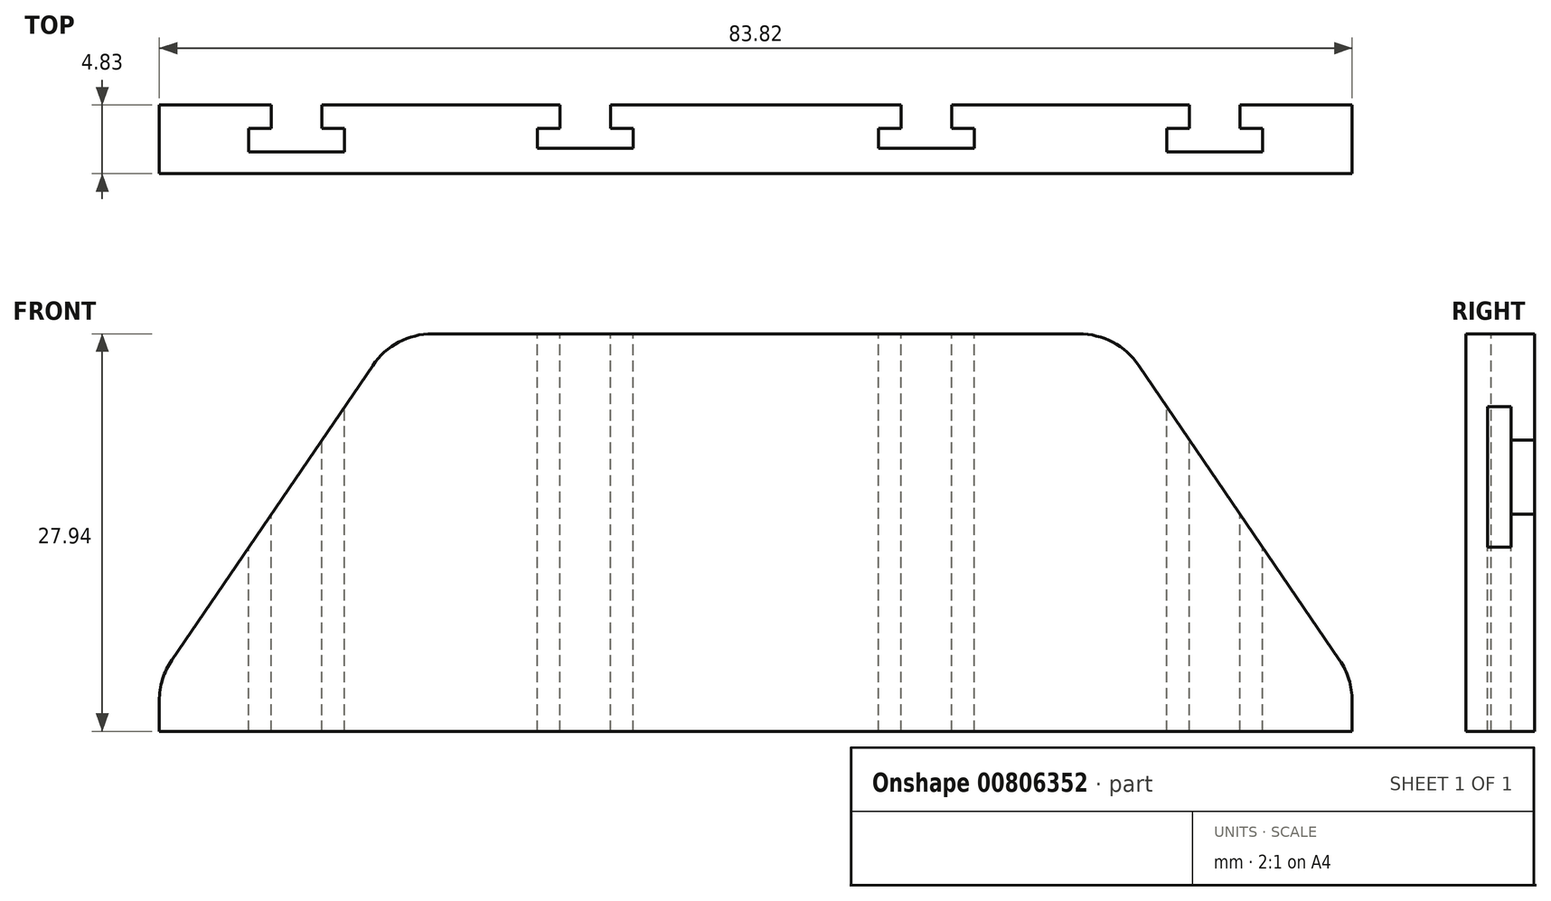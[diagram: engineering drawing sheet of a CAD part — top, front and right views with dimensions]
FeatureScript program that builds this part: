
annotation { "Feature Type Name" : "Feature", "Feature Type Description" : "" }
export const myFeature = defineFeature(function(context is Context, id is Id, definition is map)
    precondition{}
    {
        {
            var Q0;
            Q0=qCreatedBy(makeId("Front.planeOp"),FACE);
            var sketch = newSketch(context, id + "F0", { "sketchPlane" : qUnion([Q0])});
            skLineSegment(sketch, "E0", {"start": v(-44.45, -15.52) * mm, "end": v(-25.4, 12.42) * mm});
            skLineSegment(sketch, "E1", {"start": v(-25.4, 12.42) * mm, "end": v(25.4, 12.42) * mm});
            skLineSegment(sketch, "E2", {"start": v(25.4, 12.42) * mm, "end": v(44.45, -15.52) * mm});
            skLineSegment(sketch, "E3", {"start": v(44.45, -15.52) * mm, "end": v(-44.45, -15.52) * mm});
            skPoint(sketch, "E4", {"position": v(0, 12.42) * mm});
            skLineSegment(sketch, "E5.0", {"start": v(-23.39, 8.6) * mm, "end": v(23.39, 8.6) * mm});
            skLineSegment(sketch, "E5.1", {"start": v(-37.24, -11.71) * mm, "end": v(-23.39, 8.6) * mm});
            skLineSegment(sketch, "E5.2", {"start": v(37.24, -11.71) * mm, "end": v(-37.24, -11.71) * mm});
            skLineSegment(sketch, "E5.3", {"start": v(23.39, 8.6) * mm, "end": v(37.24, -11.71) * mm});
            skLineSegment(sketch, "E6", {"start": v(41.91, -1.58) * mm, "end": v(41.91, -22.95) * mm});
            skLineSegment(sketch, "E7.MirrorCS", {"start": v(-41.91, -1.58) * mm, "end": v(-41.91, -22.95) * mm});
            skSolve(sketch);
        }
        {
            var Q0;
            {var subQ1=sQuery(id+"F0.wireOp",EDGE,"E1");Q0=makeQuery(id+"F0.imprint","IMPRINT",FACE,{"disambiguationData":[TD([[makeQuery(id+"F0.imprint","IMPRINT",EDGE,{"derivedFrom":subQ1}),-1.0]])]});}
            var Q1;
            Q1=makeQuery(id+"F0.imprint","IMPRINT",FACE,{"disambiguationData":[TD([[makeQuery(id+"F0.imprint","IMPRINT",EDGE,{"derivedFrom":sQuery(id+"F0.wireOp",EDGE,"E5.2")}),1.0]])]});
            var Q2;
            Q2=makeQuery(id+"F0.imprint","IMPRINT",FACE,{"disambiguationData":[TD([[makeQuery(id+"F0.imprint","IMPRINT",EDGE,{"derivedFrom":sQuery(id+"F0.wireOp",EDGE,"E5.0")}),-1.0]])]});
            extrude(context, id + "F1", {"entities" : qUnion([Q0, Q1, Q2]), "depth" : 4.83 * mm, "offsetDistance" : 25.4 * mm});
        }
        {
            var Q0;
            Q0=qCreatedBy(makeId("Top.planeOp"),FACE);
            var sketch = newSketch(context, id + "F2", { "sketchPlane" : qUnion([Q0])});
            skLineSegment(sketch, "E8.bottom", {"start": v(13.77, 0) * mm, "end": v(10.21, 0) * mm});
            skLineSegment(sketch, "E8.top", {"start": v(13.77, -1.65) * mm, "end": v(10.21, -1.65) * mm});
            skLineSegment(sketch, "E8.left", {"start": v(13.77, 0) * mm, "end": v(13.77, -1.65) * mm});
            skLineSegment(sketch, "E8.right", {"start": v(10.21, 0) * mm, "end": v(10.21, -1.65) * mm});
            skLineSegment(sketch, "E9.bottom", {"start": v(15.35, -1.65) * mm, "end": v(8.62, -1.65) * mm});
            skLineSegment(sketch, "E9.top", {"start": v(15.35, -3.05) * mm, "end": v(8.62, -3.05) * mm});
            skLineSegment(sketch, "E9.left", {"start": v(15.35, -1.65) * mm, "end": v(15.35, -3.05) * mm});
            skLineSegment(sketch, "E9.right", {"start": v(8.62, -1.65) * mm, "end": v(8.62, -3.05) * mm});
            skPoint(sketch, "E10", {"position": v(11.99, -3.05) * mm});
            skPoint(sketch, "E11", {"position": v(11.99, -1.65) * mm});
            skLineSegment(sketch, "E12.MirrorCS", {"start": v(-13.77, -1.65) * mm, "end": v(-10.21, -1.65) * mm});
            skLineSegment(sketch, "E13.MirrorCS", {"start": v(-13.77, 0) * mm, "end": v(-13.77, -1.65) * mm});
            skLineSegment(sketch, "E14.MirrorCS", {"start": v(-10.21, 0) * mm, "end": v(-10.21, -1.65) * mm});
            skLineSegment(sketch, "E15.MirrorCS", {"start": v(-15.35, -1.65) * mm, "end": v(-15.35, -3.05) * mm});
            skLineSegment(sketch, "E16.MirrorCS", {"start": v(-8.62, -1.65) * mm, "end": v(-8.62, -3.05) * mm});
            skLineSegment(sketch, "E17.MirrorCS", {"start": v(-15.35, -1.65) * mm, "end": v(-8.62, -1.65) * mm});
            skLineSegment(sketch, "E18.MirrorCS", {"start": v(-15.35, -3.05) * mm, "end": v(-8.62, -3.05) * mm});
            skPoint(sketch, "E19.MirrorP", {"position": v(-11.99, -3.05) * mm});
            skLineSegment(sketch, "E20.MirrorCS", {"start": v(-13.77, 0) * mm, "end": v(-10.21, 0) * mm});
            skPoint(sketch, "E21.MirrorP", {"position": v(-11.99, -1.65) * mm});
            skSolve(sketch);
        }
        {
            var Q0;
            {var subQ4=sQuery(id+"F2.wireOp",EDGE,"E12.MirrorCS");var subQ5=makeQuery(id+"F2.imprint","IMPRINT",EDGE,{"derivedFrom":subQ4});var subQ9=sQuery(id+"F2.wireOp",EDGE,"E8.top");var subQ13=makeQuery(id+"F2.imprint","IMPRINT",EDGE,{"derivedFrom":subQ9});Q0=qUnion([makeQuery(id+"F2.imprint","IMPRINT",FACE,{"disambiguationData":[TD([[makeQuery(id+"F2.imprint","IMPRINT",EDGE,{"derivedFrom":sQuery(id+"F2.wireOp",EDGE,"E8.bottom")}),1.0]])]}),makeQuery(id+"F2.imprint","IMPRINT",FACE,{"disambiguationData":[TD([[subQ13,1.0]])]}),makeQuery(id+"F2.imprint","IMPRINT",FACE,{"disambiguationData":[TD([[subQ5,1.0]])]}),makeQuery(id+"F2.imprint","IMPRINT",FACE,{"disambiguationData":[TD([[subQ5,-1.0]])]})]);}
            extrude(context, id + "F3", {"entities" : qUnion([Q0]), "operationType" : NewBodyOperationType.REMOVE, "endBound" : BoundingType.SYMMETRIC, "oppositeDirection" : true, "depth" : 50.8 * mm, "offsetDistance" : 25.4 * mm});
        }
        {
            var Q0;
            Q0=qCreatedBy(makeId("Top.planeOp"),FACE);
            cPlane(context, id + "F4", {"entities" : qUnion([Q0]), "cplaneType" : CPlaneType.OFFSET, "offset" : 12.7 * mm, "width" : 152.4 * mm, "height" : 152.4 * mm});
        }
        {
            var Q0;
            Q0=qCreatedBy(id+"F4.planeOp",FACE);
            var sketch = newSketch(context, id + "F5", { "sketchPlane" : qUnion([Q0])});
            skLineSegment(sketch, "E22.bottom", {"start": v(34.04, 0) * mm, "end": v(30.48, 0) * mm});
            skLineSegment(sketch, "E22.top", {"start": v(34.04, -1.65) * mm, "end": v(30.48, -1.65) * mm});
            skLineSegment(sketch, "E22.left", {"start": v(34.04, 0) * mm, "end": v(34.04, -1.65) * mm});
            skLineSegment(sketch, "E22.right", {"start": v(30.48, 0) * mm, "end": v(30.48, -1.65) * mm});
            skLineSegment(sketch, "E23.bottom", {"start": v(35.62, -1.65) * mm, "end": v(28.9, -1.65) * mm});
            skLineSegment(sketch, "E23.top", {"start": v(35.62, -3.3) * mm, "end": v(28.9, -3.3) * mm});
            skLineSegment(sketch, "E23.left", {"start": v(35.62, -1.65) * mm, "end": v(35.62, -3.3) * mm});
            skLineSegment(sketch, "E23.right", {"start": v(28.9, -1.65) * mm, "end": v(28.9, -3.3) * mm});
            skPoint(sketch, "E24", {"position": v(32.26, -3.3) * mm});
            skPoint(sketch, "E25", {"position": v(32.26, -1.65) * mm});
            skLineSegment(sketch, "E26.MirrorCS", {"start": v(-34.04, 0) * mm, "end": v(-34.04, -1.65) * mm});
            skLineSegment(sketch, "E27.MirrorCS", {"start": v(-35.62, -1.65) * mm, "end": v(-35.62, -3.3) * mm});
            skLineSegment(sketch, "E28.MirrorCS", {"start": v(-34.04, 0) * mm, "end": v(-30.48, 0) * mm});
            skLineSegment(sketch, "E29.MirrorCS", {"start": v(-34.04, -1.65) * mm, "end": v(-30.48, -1.65) * mm});
            skLineSegment(sketch, "E30.MirrorCS", {"start": v(-30.48, 0) * mm, "end": v(-30.48, -1.65) * mm});
            skLineSegment(sketch, "E31.MirrorCS", {"start": v(-35.62, -1.65) * mm, "end": v(-28.9, -1.65) * mm});
            skLineSegment(sketch, "E32.MirrorCS", {"start": v(-35.62, -3.3) * mm, "end": v(-28.9, -3.3) * mm});
            skLineSegment(sketch, "E33.MirrorCS", {"start": v(-28.9, -1.65) * mm, "end": v(-28.9, -3.3) * mm});
            skPoint(sketch, "E34.MirrorP", {"position": v(-32.26, -1.65) * mm});
            skPoint(sketch, "E35.MirrorP", {"position": v(-32.26, -3.3) * mm});
            skSolve(sketch);
        }
        {
            var Q0;
            Q0=makeQuery(id+"F5.imprint","IMPRINT",FACE,{"disambiguationData":[TD([[makeQuery(id+"F5.imprint","IMPRINT",EDGE,{"derivedFrom":sQuery(id+"F5.wireOp",EDGE,"E26.MirrorCS")}),1.0]])]});
            var Q1;
            {var subQ3=sQuery(id+"F5.wireOp",EDGE,"E27.MirrorCS");Q1=makeQuery(id+"F5.imprint","IMPRINT",FACE,{"disambiguationData":[TD([[makeQuery(id+"F5.imprint","IMPRINT",EDGE,{"derivedFrom":subQ3}),1.0]])]});}
            var Q2;
            Q2=makeQuery(id+"F5.imprint","IMPRINT",FACE,{"disambiguationData":[TD([[makeQuery(id+"F5.imprint","IMPRINT",EDGE,{"derivedFrom":sQuery(id+"F5.wireOp",EDGE,"E22.bottom")}),1.0]])]});
            var Q3;
            {var subQ1=sQuery(id+"F5.wireOp",EDGE,"E22.top");Q3=makeQuery(id+"F5.imprint","IMPRINT",FACE,{"disambiguationData":[TD([[makeQuery(id+"F5.imprint","IMPRINT",EDGE,{"derivedFrom":subQ1}),1.0]])]});}
            extrude(context, id + "F6", {"entities" : qUnion([Q0, Q1, Q2, Q3]), "operationType" : NewBodyOperationType.REMOVE, "oppositeDirection" : true, "depth" : 50.8 * mm, "offsetDistance" : 25.4 * mm});
        }
        {
            var Q0;
            Q0=makeQuery(id+"F1.opExtrude","SWEPT_EDGE",EDGE,{"disambiguationData":[OSD([sQuery(id+"F0.wireOp",EDGE,"E0"),sQuery(id+"F0.wireOp",EDGE,"E7.MirrorCS")])]});
            var Q1;
            Q1=makeQuery(id+"F1.opExtrude","SWEPT_EDGE",EDGE,{"disambiguationData":[OSD([sQuery(id+"F0.wireOp",EDGE,"E2"),sQuery(id+"F0.wireOp",EDGE,"E6")])]});
            fillet(context, id + "F7", {"entities" : qUnion([Q0, Q1]), "radius" : 5.08 * mm, "tangentPropagation" : true, "allowEdgeOverflow" : false});
        }
        {
            var Q0;
            Q0=makeQuery(id+"F1.opExtrude","SWEPT_EDGE",EDGE,{"disambiguationData":[OSD([sQuery(id+"F0.wireOp",EDGE,"E0"),sQuery(id+"F0.wireOp",EDGE,"E1")])]});
            var Q1;
            Q1=makeQuery(id+"F1.opExtrude","SWEPT_EDGE",EDGE,{"disambiguationData":[OSD([sQuery(id+"F0.wireOp",EDGE,"E1"),sQuery(id+"F0.wireOp",EDGE,"E2")])]});
            fillet(context, id + "F8", {"entities" : qUnion([Q0, Q1]), "radius" : 5.08 * mm, "tangentPropagation" : true, "allowEdgeOverflow" : false});
        }
    });
